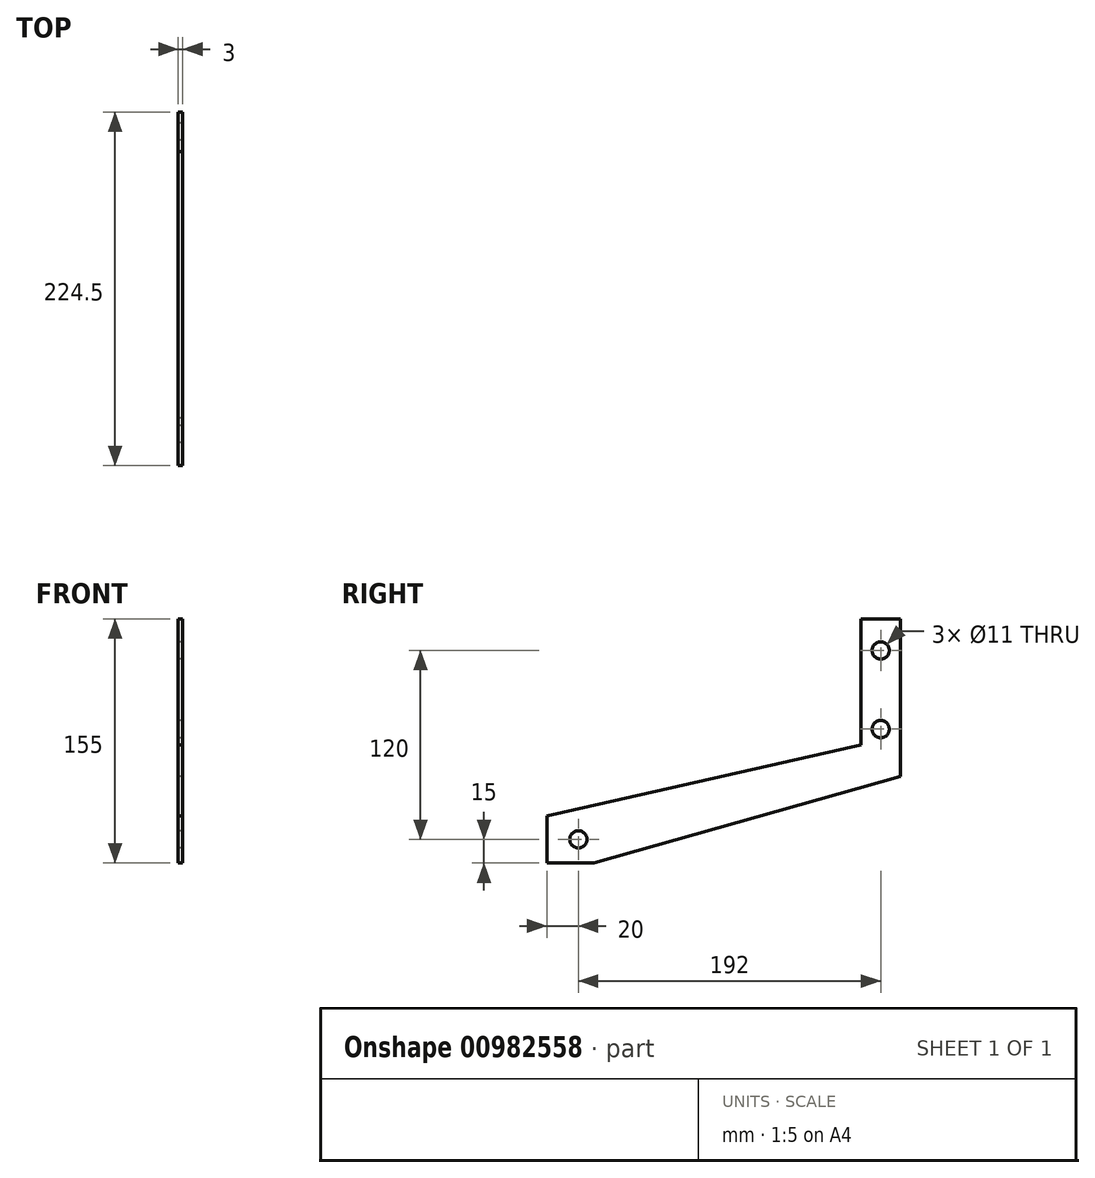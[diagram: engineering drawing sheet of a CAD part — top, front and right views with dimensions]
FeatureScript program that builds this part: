
annotation { "Feature Type Name" : "Feature", "Feature Type Description" : "" }
export const myFeature = defineFeature(function(context is Context, id is Id, definition is map)
    precondition{}
    {
        {
            var Q0;
            Q0=qCreatedBy(makeId("Right.planeOp"),FACE);
            var sketch = newSketch(context, id + "F0", { "sketchPlane" : qUnion([Q0])});
            skLineSegment(sketch, "E0", {"start": v(0, 0) * mm, "end": v(0, 100) * mm});
            skLineSegment(sketch, "E1", {"start": v(0, 100) * mm, "end": v(-25, 100) * mm});
            skLineSegment(sketch, "E2", {"start": v(-25, 100) * mm, "end": v(-25, 20) * mm});
            skLineSegment(sketch, "E3", {"start": v(-25, 20) * mm, "end": v(-224.5, -25) * mm});
            skLineSegment(sketch, "E4", {"start": v(-224.5, -25) * mm, "end": v(-224.5, -55) * mm});
            skLineSegment(sketch, "E5", {"start": v(-224.5, -55) * mm, "end": v(-194.5, -55) * mm});
            skLineSegment(sketch, "E6", {"start": v(0, 0) * mm, "end": v(-194.5, -55) * mm});
            skPoint(sketch, "E7", {"position": v(-12.5, 80) * mm});
            skCircle(sketch, "E8", {"center": v(-12.5, 80) * mm, "radius": 5.5 * mm});
            skPoint(sketch, "E9", {"position": v(-12.5, 30) * mm});
            skCircle(sketch, "E10", {"center": v(-12.5, 30) * mm, "radius": 5.5 * mm});
            skCircle(sketch, "E11", {"center": v(-204.5, -40) * mm, "radius": 5.5 * mm});
            skSolve(sketch);
        }
        {
            var Q0;
            Q0=makeQuery(id+"F0.imprint","IMPRINT",FACE,{"disambiguationData":[TD([[makeQuery(id+"F0.imprint","IMPRINT",EDGE,{"derivedFrom":sQuery(id+"F0.wireOp",EDGE,"E0")}),1.0]])]});
            extrude(context, id + "F1", {"entities" : qUnion([Q0]), "endBound" : BoundingType.SYMMETRIC, "depth" : 3 * mm, "offsetDistance" : 25 * mm});
        }
    });
